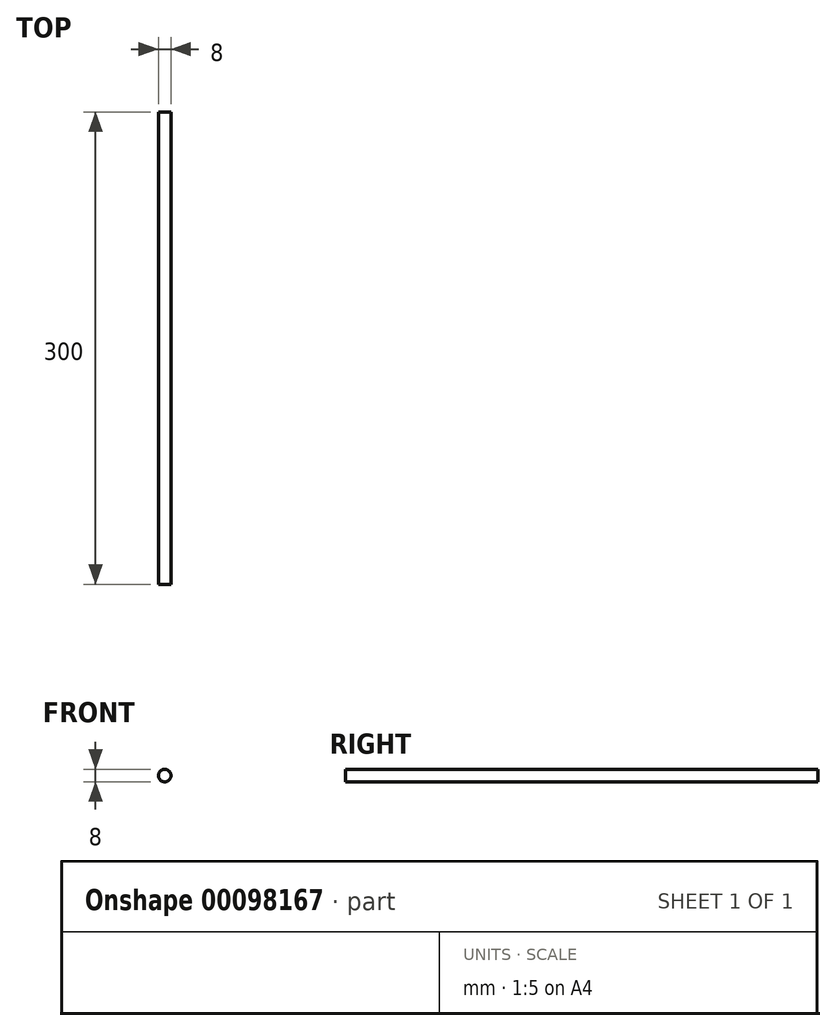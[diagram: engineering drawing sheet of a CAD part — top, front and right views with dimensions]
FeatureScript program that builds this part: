
annotation { "Feature Type Name" : "Feature", "Feature Type Description" : "" }
export const myFeature = defineFeature(function(context is Context, id is Id, definition is map)
    precondition{}
    {
        {
            var Q0;
            Q0=qCreatedBy(makeId("Front.planeOp"),FACE);
            var sketch = newSketch(context, id + "F0", { "sketchPlane" : qUnion([Q0])});
            skCircle(sketch, "E0", {"center": v(-41.14, 40.28) * mm, "radius": 4 * mm});
            skSolve(sketch);
        }
        {
            var Q0;
            Q0=makeQuery(id+"F0.imprint","IMPRINT",FACE,{"disambiguationData":[TD([[makeQuery(id+"F0.imprint","IMPRINT",EDGE,{"derivedFrom":sQuery(id+"F0.wireOp",EDGE,"E0")}),1.0]])]});
            extrude(context, id + "F1", {"entities" : qUnion([Q0]), "depth" : 300 * mm});
        }
    });
